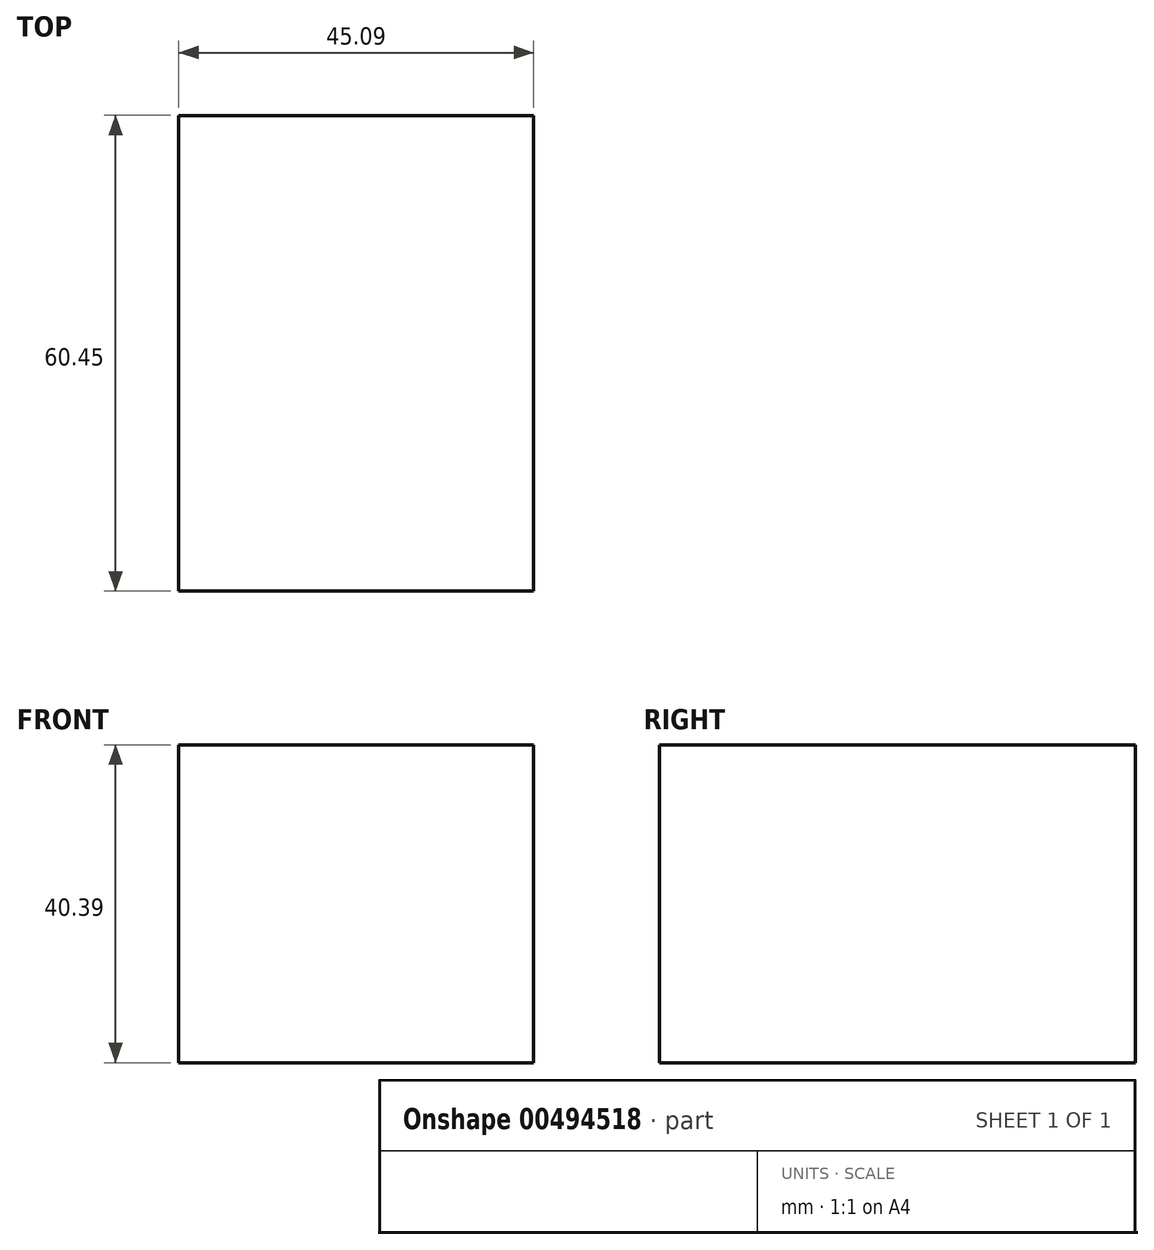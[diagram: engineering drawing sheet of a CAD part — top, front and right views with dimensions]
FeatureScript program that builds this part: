
annotation { "Feature Type Name" : "Feature", "Feature Type Description" : "" }
export const myFeature = defineFeature(function(context is Context, id is Id, definition is map)
    precondition{}
    {
        {
            var Q0;
            Q0=qCreatedBy(makeId("Top.planeOp"),FACE);
            var sketch = newSketch(context, id + "F0", { "sketchPlane" : qUnion([Q0])});
            skLineSegment(sketch, "E0.bottom", {"start": v(-11.33, -48.3) * mm, "end": v(33.76, -48.3) * mm});
            skLineSegment(sketch, "E0.top", {"start": v(-11.33, 12.16) * mm, "end": v(33.76, 12.16) * mm});
            skLineSegment(sketch, "E0.left", {"start": v(-11.33, -48.3) * mm, "end": v(-11.33, 12.16) * mm});
            skLineSegment(sketch, "E0.right", {"start": v(33.76, -48.3) * mm, "end": v(33.76, 12.16) * mm});
            skSolve(sketch);
        }
        {
            var Q0;
            Q0=makeQuery(id+"F0.imprint","IMPRINT",FACE,{"disambiguationData":[TD([[makeQuery(id+"F0.imprint","IMPRINT",EDGE,{"derivedFrom":sQuery(id+"F0.wireOp",EDGE,"E0.bottom")}),1.0]])]});
            extrude(context, id + "F1", {"entities" : qUnion([Q0]), "depth" : 40.4 * mm});
        }
    });
